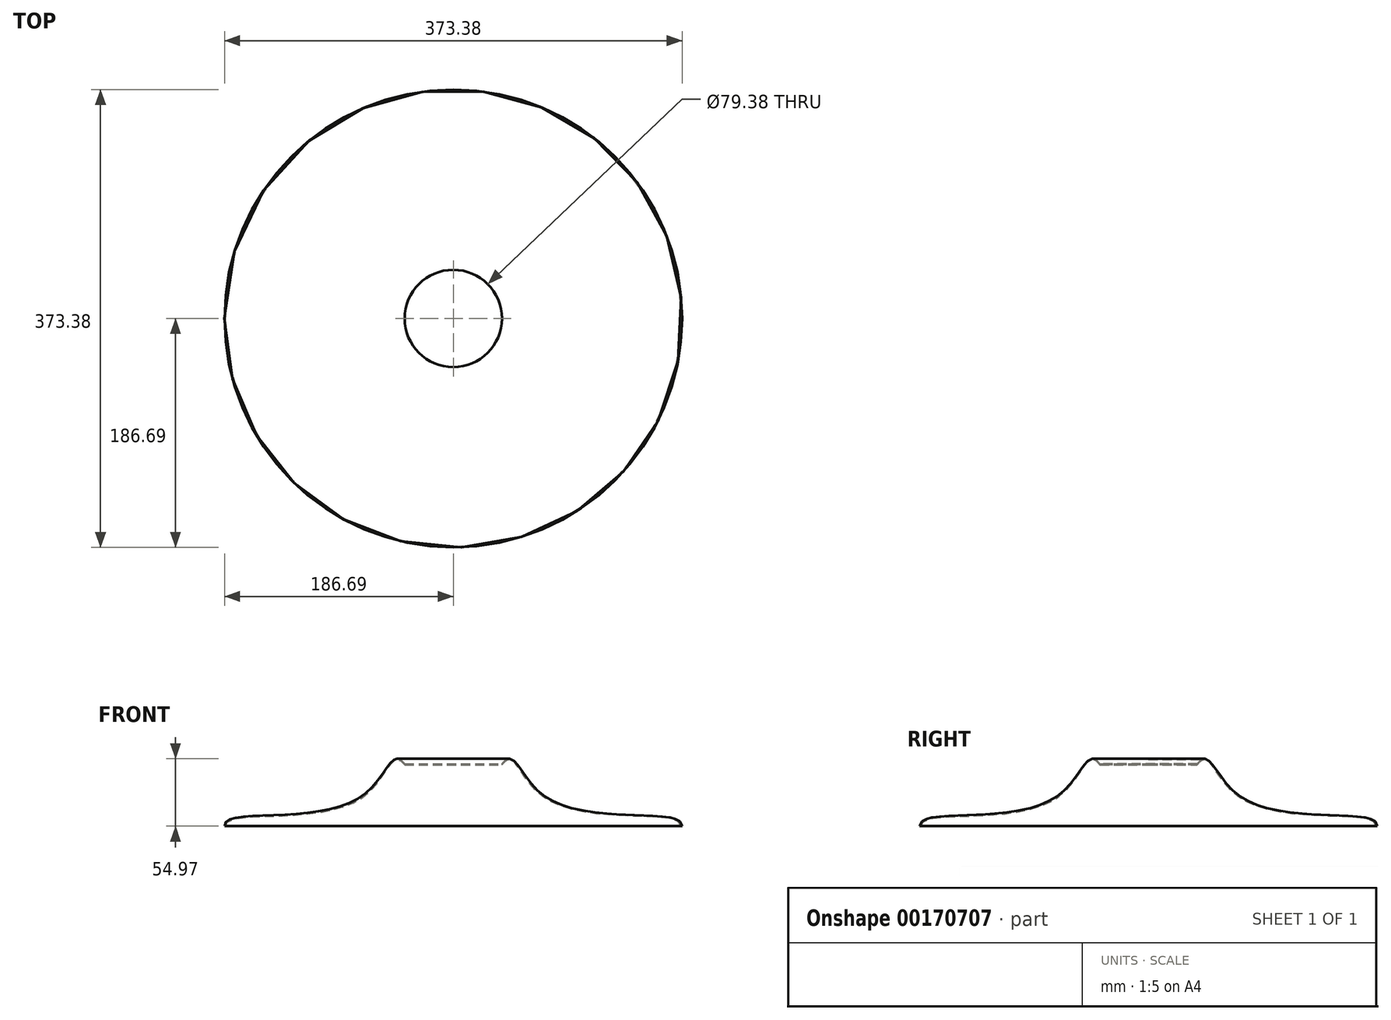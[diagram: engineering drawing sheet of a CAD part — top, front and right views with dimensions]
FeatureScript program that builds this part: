
annotation { "Feature Type Name" : "Feature", "Feature Type Description" : "" }
export const myFeature = defineFeature(function(context is Context, id is Id, definition is map)
    precondition{}
    {
        {
            var Q0;
            Q0=qCreatedBy(makeId("Front.planeOp"),FACE);
            var sketch = newSketch(context, id + "F0", { "sketchPlane" : qUnion([Q0])});
            skLineSegment(sketch, "E0", {"start": v(0, 0) * mm, "end": v(0, 50.04) * mm, "construction": true});
            skLineSegment(sketch, "E1", {"start": v(0, 0) * mm, "end": v(186.7, 0) * mm, "construction": true});
            skLineSegment(sketch, "E2", {"start": v(0, 50.04) * mm, "end": v(39.69, 50.04) * mm, "construction": true});
            skLineSegment(sketch, "E3", {"start": v(0, 50.04) * mm, "end": v(0, 50.83) * mm, "construction": true});
            skLineSegment(sketch, "E4", {"start": v(0, 50.83) * mm, "end": v(39.69, 50.83) * mm, "construction": true});
            skLineSegment(sketch, "E5", {"start": v(39.69, 50.83) * mm, "end": v(39.69, 50.04) * mm});
            skLineSegment(sketch, "E6", {"start": v(186.7, 0) * mm, "end": v(185.9, 0) * mm});
            skFitSpline(sketch, "E7", {"points": [v(185.9, 0) * mm, v(154.2, 7.95) * mm, v(73.12, 24.05) * mm, v(47.73, 53.84) * mm, v(39.69, 50.04) * mm], "startDerivative": vector(-11.45, 85.64) * mm, "endDerivative": vector(-72.45, -90.71) * mm});
            skFitSpline(sketch, "E8", {"points": [v(39.69, 50.83) * mm, v(47.73, 54.54) * mm, v(73.12, 25.43) * mm, v(154.2, 8.78) * mm, v(186.7, 0) * mm], "startDerivative": vector(60.2, 77.5) * mm, "endDerivative": vector(-2.07, -93.26) * mm});
            skSolve(sketch);
        }
        {
            var Q0;
            Q0=makeQuery(id+"F0.imprint","IMPRINT",FACE,{"disambiguationData":[TD([[makeQuery(id+"F0.imprint","IMPRINT",EDGE,{"derivedFrom":sQuery(id+"F0.wireOp",EDGE,"E5")}),1.0]])]});
            var Q1;
            Q1=sQuery(id+"F0.wireOp",EDGE,"E0");
            revolve(context, id + "F1", {"entities" : qUnion([Q0]), "axis" : qUnion([Q1]), "revolveType" : RevolveType.FULL});
        }
    });
